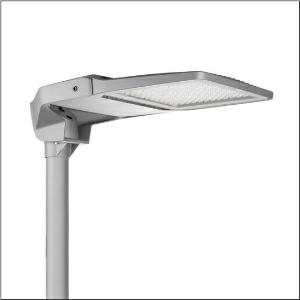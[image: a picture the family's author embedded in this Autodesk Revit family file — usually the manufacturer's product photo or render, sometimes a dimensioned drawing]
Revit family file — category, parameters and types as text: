
# Revit family: floodlight_fl_20_midi___pl52_5xa7682d3d4ac_aece
name_source: partatom
category: Lighting Fixtures
units: mm (PartAtom-declared; Revit-internal decimal feet)

## family parameters
Cut with Voids When Loaded = No
Host = Face
Light Source = No
Part Type = Normal
Room Calculation Point = No
Round Connector Dimension = Use Diameter
Shared = No

## types (1)
- --- (1 x LED 5000K / CRI = 70 (unbekannt), 18250 lm, 5000K)
    Apparent Load = 142 VA
    CIE Flux Codes = 27 59 98 100 100
    Color Rendering = 70
    Color Temperature = 5000K
    Default Elevation = 1800 mm
    Description = Floodlight FL 20 midi, floodlight, primary light control with lens, of plastic, primary optical cover: protective disc, of toughened safety glass, transparent, light distribution: PL52, light emission: direct distribution, primary light characteristic: asymmetric, installation type: side-entry, post-top, LED, High Power LED, rated luminous flux: 18.250lm, luminous efficacy: 129lm/W, light colour: 750, colour temperature: 5000K, control gear: ECG Plus, control: flexible luminous flux parameterisation, time-dependent luminous flux control, digital communication interface, overheat protection, power reduction, electronic power reduction, with terminal, 5-pole, max. 2.5mm², mains connection: 220..240V, AC, 50/60Hz, rated input power: 142W, LED unit, of diecast aluminium, powder-coated, Siteco® metallic grey (DB 702S), corrosivity category C5 mid according to DIN EN ISO 12944, please order mast flange separately, incl. 1x M20 cable gland for cable Ø 6.5..12mm, inclination adjustable: 0°, 3°, 8°, 15°, length: 862mm, width: 450mm, height: 176mm, housing frame, of diecast aluminium, powder-coated, Siteco® metallic grey (DB 702S), mast flange adapter, of diecast aluminium, powder-coated, Siteco® metallic grey (DB 702S), DALI, protection rating (complete): IP66, insulation class (complete): insulation class II (safety insulation), certification: CE, ENEC, VDE, protection symbol: D, permissible operating ambient temperature: -40..+40°C, permissible operating ambient temperature for outdoor applications: -40..+50°C, standard: DIN EN 12944, packaging unit: 1 piece

Light Distribution: PL52
    Height = 76 mm
    Lamp = 1 x LED 5000K / CRI >= 70 (unbekannt)
    Lamp Light Flux = 18250 lm
    Lamp count = 1
    Length = 862 mm
    Luminous efficacy = 129 lm/W
    Manufacturer = Siteco
    ModVariant = No
    Model = 5XA7682D3D4AC
    Number of Poles = 1
    OnlyDefault = Yes
    Power Factor = 1
    Product Name = Floodlight FL 20 midi | PL52
    Product group = floodlight | pylon top
    ProductGroupID = 6101
    Protection Class = Protection class II
    Protection Degree = IP 66
    RLX_Detail_Level = 1
    RLX_Emergency_Light_Flux = 0 lm
    RLX_Emergency_Type = 0
    RLX_Emergency_Type_DB = No
    RlxData = <blob elided: 118317 chars, md5=d9d5b889>
    Socket = socket
    Standby Power = 0 W
    System Light Flux = 18250 lm
    System Power = 142 W
    Type Comments = factory setting: luminous flux: 100 % | dim-lin: 254 | 489 mA
    Type Image = l_1005941.jpg
    URL = http://relux.com
    VarID = @adj_147751
    Voltage = 0 V
    Weight = 0.00 kg
    Width = 450 mm

## geometry (parser evidence)
native form markers: Blend x4, Sweep x12
no freeform markers — native parametric forms only
